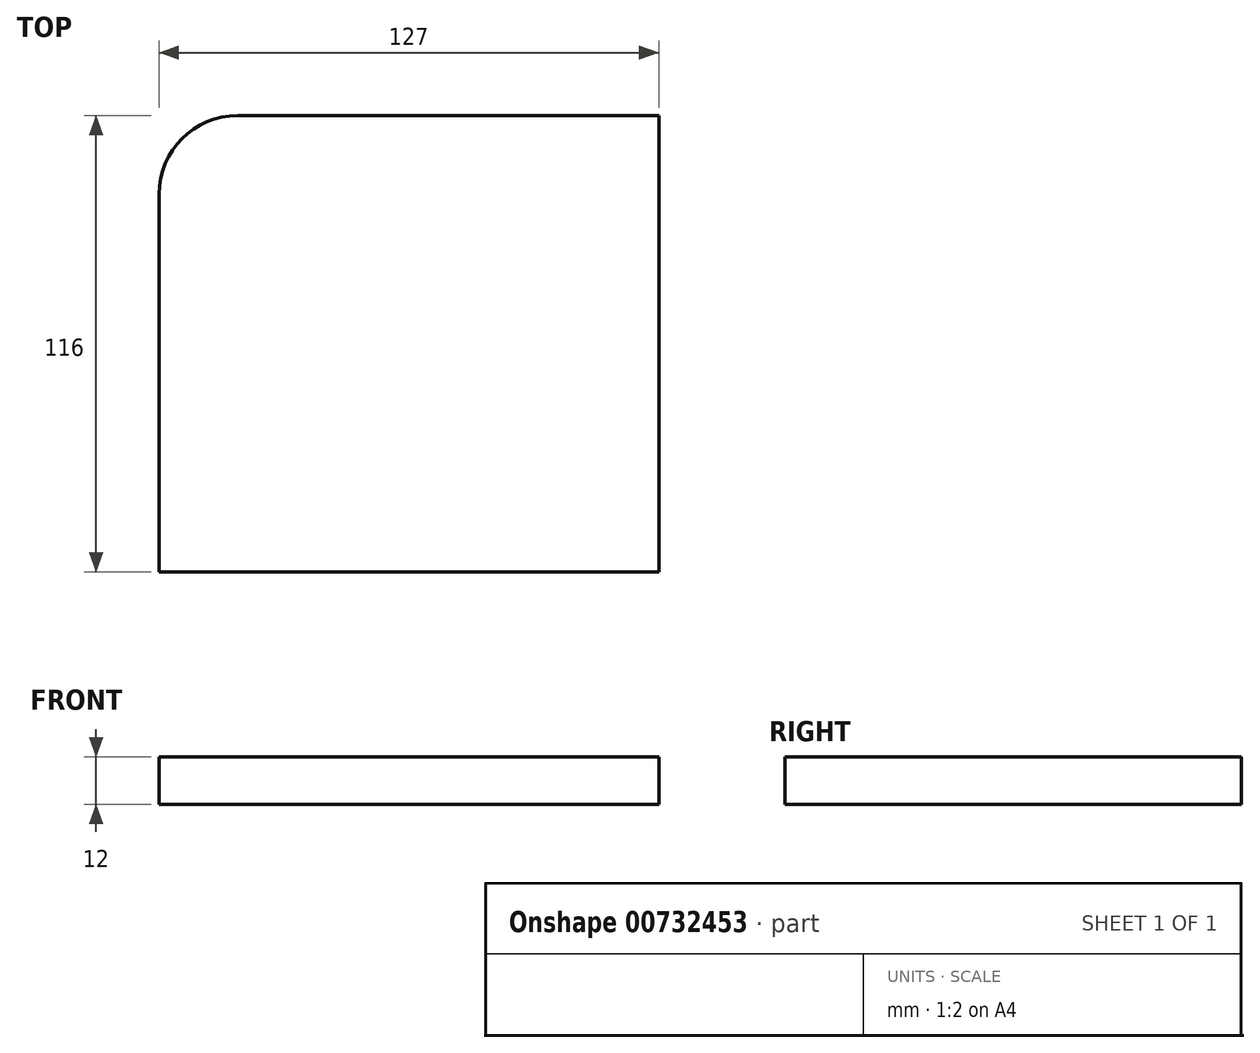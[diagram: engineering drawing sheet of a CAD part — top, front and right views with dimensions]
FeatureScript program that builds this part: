
annotation { "Feature Type Name" : "Feature", "Feature Type Description" : "" }
export const myFeature = defineFeature(function(context is Context, id is Id, definition is map)
    precondition{}
    {
        {
            var Q0;
            Q0=qCreatedBy(makeId("Top.planeOp"),FACE);
            var sketch = newSketch(context, id + "F0", { "sketchPlane" : qUnion([Q0])});
            skLineSegment(sketch, "E0.bottom", {"start": v(-53.44, -58) * mm, "end": v(73.56, -58) * mm});
            skLineSegment(sketch, "E0.top", {"start": v(-53.44, 58) * mm, "end": v(73.56, 58) * mm});
            skLineSegment(sketch, "E0.left", {"start": v(-53.44, -58) * mm, "end": v(-53.44, 58) * mm});
            skLineSegment(sketch, "E0.right", {"start": v(73.56, -58) * mm, "end": v(73.56, 58) * mm});
            skPoint(sketch, "E0.middle", {"position": v(10.06, 0) * mm});
            skSolve(sketch);
        }
        {
            var Q0;
            Q0=makeQuery(id+"F0.imprint","IMPRINT",FACE,{"disambiguationData":[TD([[makeQuery(id+"F0.imprint","IMPRINT",EDGE,{"derivedFrom":sQuery(id+"F0.wireOp",EDGE,"E0.bottom")}),1.0]])]});
            extrude(context, id + "F1", {"entities" : qUnion([Q0]), "depth" : 12 * mm, "offsetDistance" : 25 * mm});
        }
        {
            var Q0;
            Q0=makeQuery(id+"F1.opExtrude","SWEPT_EDGE",EDGE,{"disambiguationData":[OSD([sQuery(id+"F0.wireOp",EDGE,"E0.top"),sQuery(id+"F0.wireOp",EDGE,"E0.left")])]});
            fillet(context, id + "F2", {"entities" : qUnion([Q0]), "radius" : 20 * mm, "tangentPropagation" : true, "allowEdgeOverflow" : false});
        }
    });
